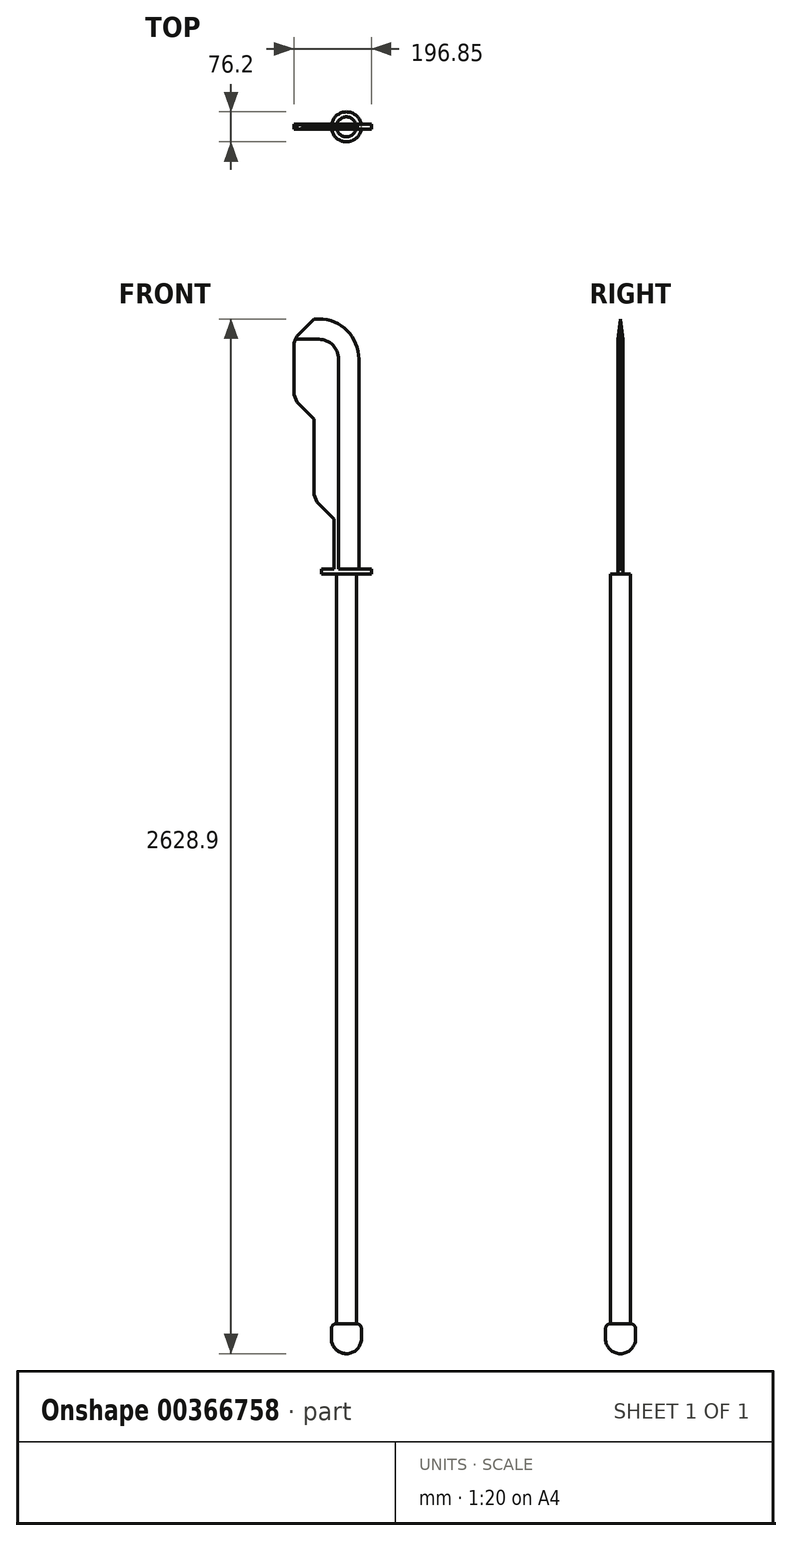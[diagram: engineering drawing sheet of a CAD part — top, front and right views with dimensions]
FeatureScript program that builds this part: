
annotation { "Feature Type Name" : "Feature", "Feature Type Description" : "" }
export const myFeature = defineFeature(function(context is Context, id is Id, definition is map)
    precondition{}
    {
        {
            var Q0;
            Q0=qCreatedBy(makeId("Top.planeOp"),FACE);
            var sketch = newSketch(context, id + "F0", { "sketchPlane" : qUnion([Q0])});
            skCircle(sketch, "E0", {"center": v(0, 0) * mm, "radius": 25.4 * mm});
            skSolve(sketch);
        }
        {
            var Q0;
            Q0 = qSketchRegion(id + "F0", true);
            extrude(context, id + "F1", {"entities" : qUnion([Q0]), "depth" : 1905 * mm});
        }
        {
            var Q0;
            Q0=makeQuery(id+"F1.opExtrude","CAP_FACE",FACE,{"disambiguationData":[OSD([sQuery(id+"F0.wireOp",EDGE,"E0")])],"isStart":true});
            var sketch = newSketch(context, id + "F2", { "sketchPlane" : qUnion([Q0])});
            skCircle(sketch, "E1", {"center": v(0, 0) * mm, "radius": 38.1 * mm});
            skSolve(sketch);
        }
        {
            var Q0;
            Q0 = qSketchRegion(id + "F2", true);
            extrude(context, id + "F3", {"entities" : qUnion([Q0]), "operationType" : NewBodyOperationType.ADD, "depth" : 76.2 * mm});
        }
        {
            var Q0;
            Q0=qCreatedBy(makeId("Front.planeOp"),FACE);
            var sketch = newSketch(context, id + "F4", { "sketchPlane" : qUnion([Q0])});
            skLineSegment(sketch, "E2", {"start": v(0, 0) * mm, "end": v(0, 1905) * mm});
            skLineSegment(sketch, "E3", {"start": v(0, 1905) * mm, "end": v(25.4, 1905) * mm});
            skLineSegment(sketch, "E4", {"start": v(0, 1905) * mm, "end": v(-25.4, 1905) * mm});
            skLineSegment(sketch, "E5", {"start": v(25.4, 1905) * mm, "end": v(63.5, 1905) * mm});
            skLineSegment(sketch, "E6", {"start": v(-25.4, 1905) * mm, "end": v(-63.5, 1905) * mm});
            skLineSegment(sketch, "E7", {"start": v(63.5, 1905) * mm, "end": v(63.5, 1917.7) * mm});
            skLineSegment(sketch, "E8", {"start": v(-63.5, 1905) * mm, "end": v(-63.5, 1917.7) * mm});
            skLineSegment(sketch, "E9", {"start": v(-63.5, 1917.7) * mm, "end": v(63.5, 1917.7) * mm});
            skLineSegment(sketch, "E10", {"start": v(63.5, 1917.7) * mm, "end": v(0, 1917.7) * mm});
            skLineSegment(sketch, "E11", {"start": v(0, 1917.7) * mm, "end": v(31.75, 1917.7) * mm});
            skLineSegment(sketch, "E12", {"start": v(31.75, 1917.7) * mm, "end": v(-63.5, 1917.7) * mm});
            skLineSegment(sketch, "E13", {"start": v(-63.5, 1917.7) * mm, "end": v(0, 1917.7) * mm});
            skLineSegment(sketch, "E14", {"start": v(0, 1917.7) * mm, "end": v(-31.75, 1917.7) * mm});
            skLineSegment(sketch, "E15", {"start": v(-31.75, 1917.7) * mm, "end": v(-31.75, 2552.7) * mm});
            skLineSegment(sketch, "E16", {"start": v(31.75, 1917.7) * mm, "end": v(31.75, 2552.7) * mm});
            skLineSegment(sketch, "E17", {"start": v(31.75, 2552.7) * mm, "end": v(-31.75, 2552.7) * mm});
            skLineSegment(sketch, "E18", {"start": v(-31.75, 2552.7) * mm, "end": v(-133.35, 2552.7) * mm});
            skLineSegment(sketch, "E19", {"start": v(-133.35, 2552.7) * mm, "end": v(-133.35, 2298.7) * mm});
            skLineSegment(sketch, "E20", {"start": v(-133.35, 2298.7) * mm, "end": v(-31.75, 2298.7) * mm});
            skLineSegment(sketch, "E21", {"start": v(-133.35, 2298.7) * mm, "end": v(-82.55, 2298.7) * mm});
            skLineSegment(sketch, "E22", {"start": v(-82.55, 2298.7) * mm, "end": v(-82.55, 2044.7) * mm});
            skLineSegment(sketch, "E23", {"start": v(-82.55, 2044.7) * mm, "end": v(-31.75, 2044.7) * mm});
            skSolve(sketch);
        }
        {
            var Q0;
            Q0 = qSketchRegion(id + "F4", true);
            extrude(context, id + "F5", {"entities" : qUnion([Q0]), "operationType" : NewBodyOperationType.ADD, "depth" : 6.35 * mm, "hasSecondDirection" : true, "secondDirectionOppositeDirection" : true, "secondDirectionDepth" : 6.35 * mm});
        }
        {
            var Q0;
            Q0=makeQuery(id+"F5.opExtrude","SWEPT_EDGE",EDGE,{"disambiguationData":[OSD([sQuery(id+"F4.wireOp",EDGE,"E19"),sQuery(id+"F4.wireOp",EDGE,"E21")])]});
            var Q1;
            Q1=makeQuery(id+"F5.opExtrude","SWEPT_EDGE",EDGE,{"disambiguationData":[OSD([sQuery(id+"F4.wireOp",EDGE,"E22"),sQuery(id+"F4.wireOp",EDGE,"E23")])]});
            chamfer(context, id + "F6", {"entities" : qUnion([Q0, Q1]), "width" : 50.8 * mm, "tangentPropagation" : true});
        }
        {
            var Q0;
            Q0=makeQuery(id+"F5.opExtrude","SWEPT_EDGE",EDGE,{"disambiguationData":[OSD([sQuery(id+"F4.wireOp",EDGE,"E16"),sQuery(id+"F4.wireOp",EDGE,"E17")])]});
            fillet(context, id + "F7", {"entities" : qUnion([Q0]), "radius" : 101.6 * mm, "tangentPropagation" : true, "allowEdgeOverflow" : false});
        }
        {
            var Q0;
            Q0=makeQuery(id+"F5.opExtrude","CAP_EDGE",EDGE,{"disambiguationData":[OSD([sQuery(id+"F4.wireOp",EDGE,"E16")])],"isStart":true});
            var Q1;
            Q1=makeQuery(id+"F5.opExtrude","CAP_EDGE",EDGE,{"disambiguationData":[OSD([sQuery(id+"F4.wireOp",EDGE,"E16")])],"isStart":false});
            chamfer(context, id + "F8", {"entities" : qUnion([Q0, Q1]), "chamferType" : ChamferType.OFFSET_ANGLE, "width" : 6.35 * mm, "oppositeDirection" : false, "angle" : 83 * degree, "tangentPropagation" : true});
        }
        {
            var Q0;
            {var subQ0=sQuery(id+"F4.wireOp",EDGE,"E19");Q0=makeQuery(id+"F6.opChamfer","BLEND_EDGE",EDGE,{"blendedFrom":[makeQuery(id+"F5.opExtrude","SWEPT_EDGE",EDGE,{"disambiguationData":[OSD([subQ0,sQuery(id+"F4.wireOp",EDGE,"E21")])]}),makeQuery(id+"F5.opExtrude","SWEPT_FACE",FACE,{"disambiguationData":[OSD([subQ0])]})],"blendedInto":[makeQuery(id+"F5.opExtrude","SWEPT_FACE",FACE,{"disambiguationData":[OSD([subQ0])]})]});}
            var Q1;
            {var subQ0=sQuery(id+"F4.wireOp",EDGE,"E22");Q1=makeQuery(id+"F6.opChamfer","BLEND_EDGE",EDGE,{"blendedFrom":[makeQuery(id+"F5.opExtrude","SWEPT_EDGE",EDGE,{"disambiguationData":[OSD([subQ0,sQuery(id+"F4.wireOp",EDGE,"E23")])]}),makeQuery(id+"F5.opExtrude","SWEPT_FACE",FACE,{"disambiguationData":[OSD([subQ0])]})],"blendedInto":[makeQuery(id+"F5.opExtrude","SWEPT_FACE",FACE,{"disambiguationData":[OSD([subQ0])]})]});}
            chamfer(context, id + "F9", {"entities" : qUnion([Q0, Q1]), "width" : 25.4 * mm, "tangentPropagation" : true});
        }
        {
            var Q0;
            Q0=makeQuery(id+"F3.opExtrude","CAP_EDGE",EDGE,{"disambiguationData":[OSD([sQuery(id+"F2.wireOp",EDGE,"E1")])],"isStart":true});
            fillet(context, id + "F10", {"entities" : qUnion([Q0]), "radius" : 12.7 * mm, "tangentPropagation" : true, "allowEdgeOverflow" : false});
        }
        {
            var Q0;
            Q0=makeQuery(id+"F3.opExtrude","CAP_EDGE",EDGE,{"disambiguationData":[OSD([sQuery(id+"F2.wireOp",EDGE,"E1")])],"isStart":false});
            fillet(context, id + "F11", {"entities" : qUnion([Q0]), "radius" : 38.1 * mm, "tangentPropagation" : true, "allowEdgeOverflow" : false});
        }
    });
